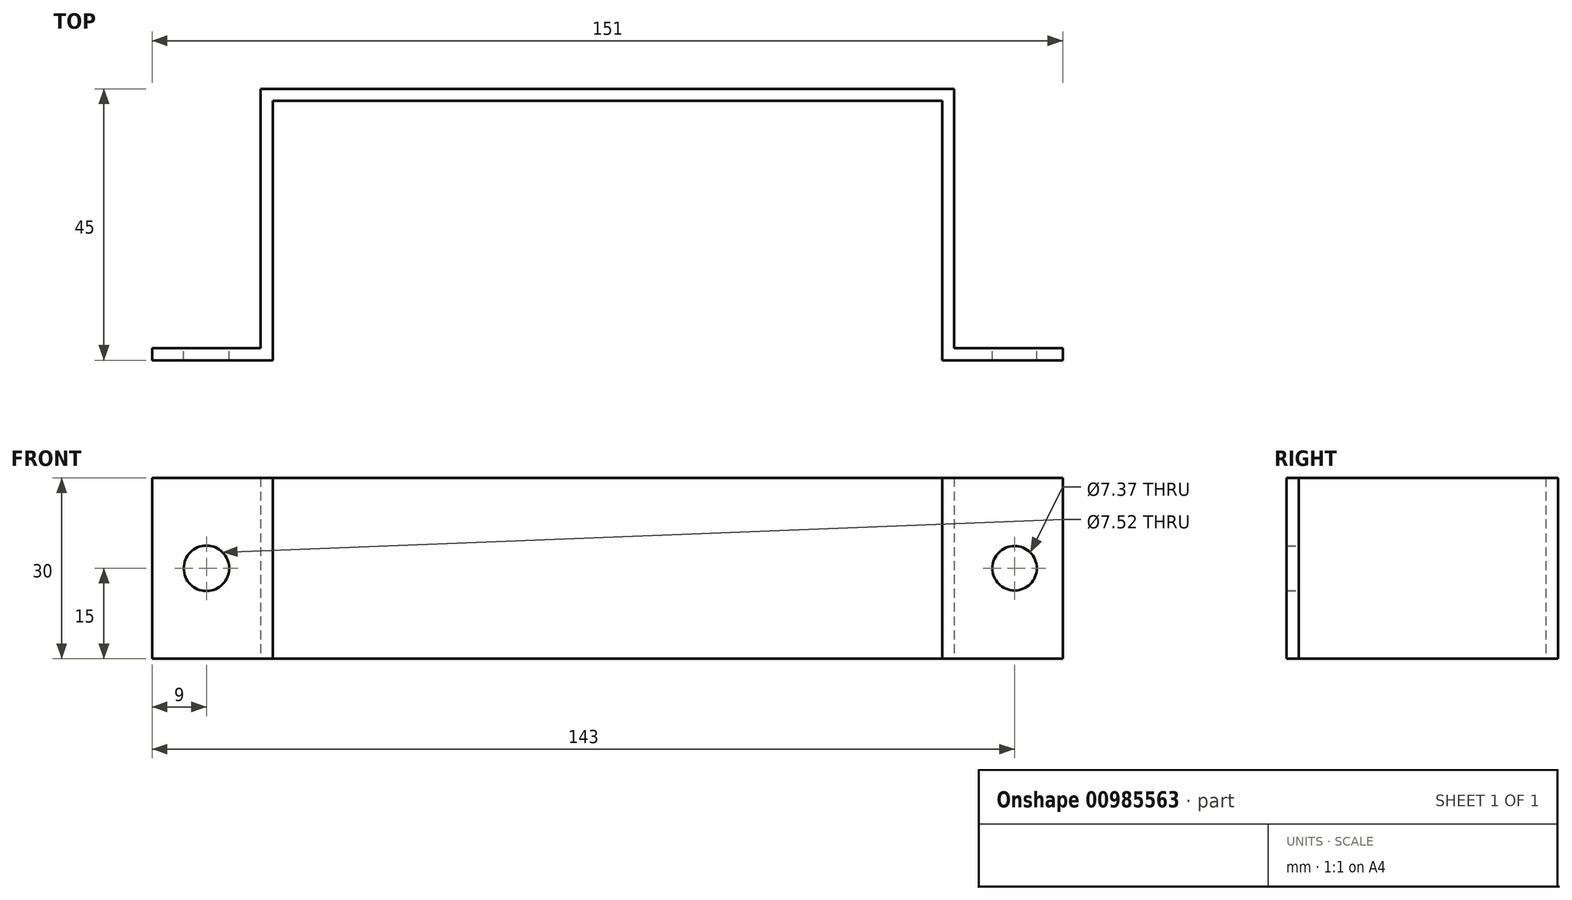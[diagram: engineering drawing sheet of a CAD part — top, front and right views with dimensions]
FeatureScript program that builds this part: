
annotation { "Feature Type Name" : "Feature", "Feature Type Description" : "" }
export const myFeature = defineFeature(function(context is Context, id is Id, definition is map)
    precondition{}
    {
        {
            var Q0;
            Q0=qCreatedBy(makeId("Top.planeOp"),FACE);
            var sketch = newSketch(context, id + "F0", { "sketchPlane" : qUnion([Q0])});
            skLineSegment(sketch, "E0", {"start": v(-29.34, 22.52) * mm, "end": v(-11.34, 22.52) * mm});
            skLineSegment(sketch, "E1", {"start": v(-11.34, 22.52) * mm, "end": v(-11.34, 65.52) * mm});
            skLineSegment(sketch, "E2", {"start": v(-11.34, 65.52) * mm, "end": v(103.66, 65.52) * mm});
            skLineSegment(sketch, "E3", {"start": v(103.66, 65.52) * mm, "end": v(103.66, 22.52) * mm});
            skLineSegment(sketch, "E4", {"start": v(103.66, 22.52) * mm, "end": v(121.66, 22.52) * mm});
            skLineSegment(sketch, "E5", {"start": v(121.66, 22.52) * mm, "end": v(121.66, 20.52) * mm});
            skLineSegment(sketch, "E6", {"start": v(121.66, 20.52) * mm, "end": v(101.66, 20.52) * mm});
            skLineSegment(sketch, "E7", {"start": v(101.66, 20.52) * mm, "end": v(101.66, 63.52) * mm});
            skLineSegment(sketch, "E8", {"start": v(101.66, 63.52) * mm, "end": v(-9.34, 63.52) * mm});
            skLineSegment(sketch, "E9", {"start": v(-9.34, 63.52) * mm, "end": v(-9.34, 20.52) * mm});
            skLineSegment(sketch, "E10", {"start": v(-9.34, 20.52) * mm, "end": v(-29.34, 20.52) * mm});
            skLineSegment(sketch, "E11", {"start": v(-29.34, 20.52) * mm, "end": v(-29.34, 22.52) * mm});
            skSolve(sketch);
        }
        {
            var Q0;
            Q0 = qSketchRegion(id + "F0", true);
            extrude(context, id + "F1", {"entities" : qUnion([Q0]), "depth" : 30 * mm, "offsetDistance" : 25.4 * mm});
        }
        {
            var Q0;
            Q0=makeQuery(id+"F1.opExtrude","SWEPT_FACE",FACE,{"disambiguationData":[OSD([sQuery(id+"F0.wireOp",EDGE,"E0")])]});
            var sketch = newSketch(context, id + "F2", { "sketchPlane" : qUnion([Q0])});
            skCircle(sketch, "E12", {"center": v(20.34, 15) * mm, "radius": 3.76 * mm});
            skPoint(sketch, "E12.centerSnap0", {"position": v(20.34, 0) * mm});
            skPoint(sketch, "E12.centerSnap1", {"position": v(29.34, 15) * mm});
            skCircle(sketch, "E13", {"center": v(-113.66, 15) * mm, "radius": 3.68 * mm});
            skSolve(sketch);
        }
        {
            var Q0;
            Q0 = qSketchRegion(id + "F2", true);
            extrude(context, id + "F3", {"entities" : qUnion([Q0]), "operationType" : NewBodyOperationType.REMOVE, "endBound" : BoundingType.THROUGH_ALL, "oppositeDirection" : true, "depth" : 25.4 * mm, "offsetDistance" : 25.4 * mm});
        }
    });
